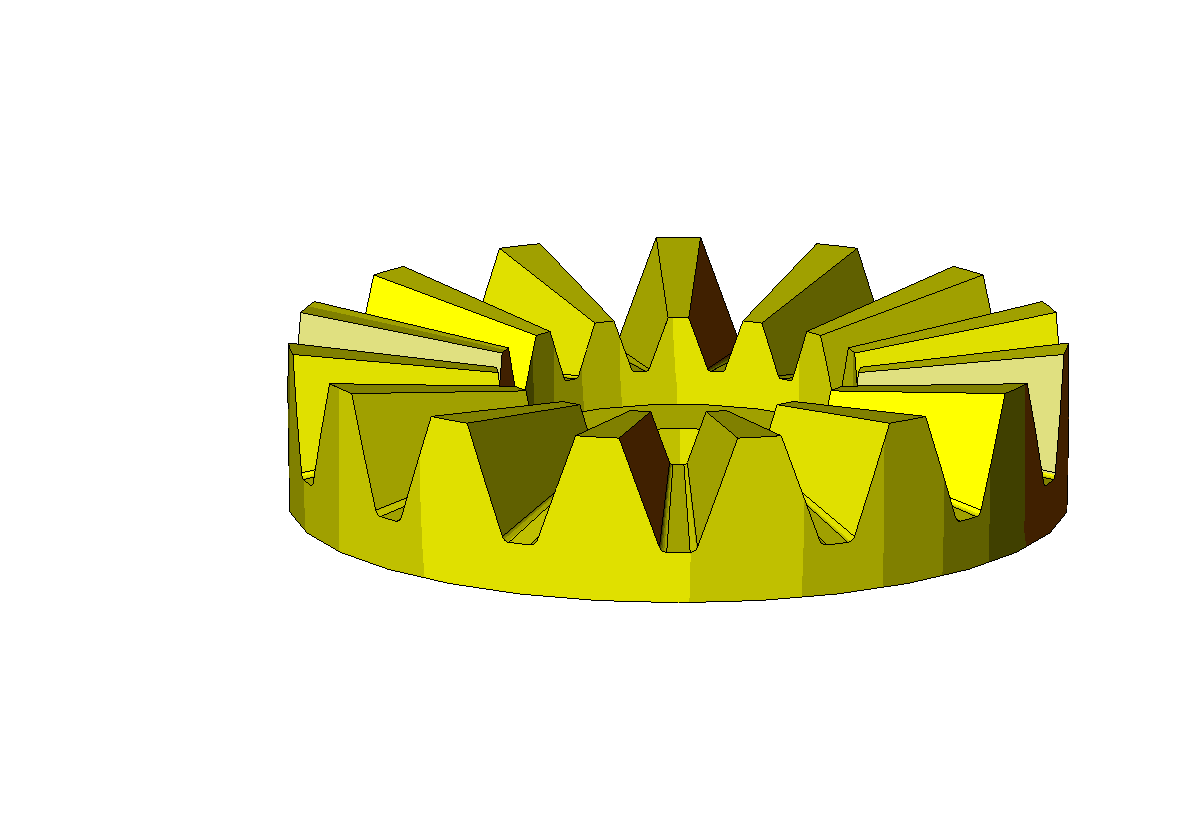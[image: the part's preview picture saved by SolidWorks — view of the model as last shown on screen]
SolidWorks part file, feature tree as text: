
SOLIDWORKS PART (.sldprt)
format: sldprt  version: not decoded by parser v0  size: 763,904 bytes
history: native  units: mm
features: plane x5, sketch x5, material x1, revolve x1, pattern_circular x1, cut_extrude x1 (+10 scaffold rows collapsed)
feature tree (24):
  scaffold x10  (default folders/planes/origin — collapsed)
  material  "Matériau <non spécifié>"
  plane  "Plan1"
  plane  "Plan de creux"
  plane  "Plan3"
  sketch  "def"  dims[c1.D1=10.0mm c1.D2=1.0mm c1.D3=1.0mm c1.D4=0.3mm c1.D5=~14.911604mm c2.D1=15.0mm c2.D6=~8.457328mm c2.D2=2.0mm c2.D7=~6.009154mm c2.D3=1.0mm c2.D8=~2.819109mm c2.D4=0.15mm c2.D5=8.0mm c3.D6=1.0mm c3.D7=85.0mm]
  sketch  "coneprimitif"  dims[c1.D1=~34.995022mm c2.D1=20.0deg c2.D2=~17.690721mm c2.D3=~34.995022mm c3.D3=~7.287182deg c3.D4=~32.161848mm c4.D4=~4.625522deg c4.D5=30.0mm c4.D1=~29.502859mm c5.D1=85.0deg c5.D2=22.0mm c5.D3=~60.444503mm c6.D3=~11.719591deg c7.D3=~64.323697mm c8.D3=~12.680383deg c8.D4=~64.323697mm c9.D4=~5.710593deg c9.D5=25.0mm c9.D6=~9.645009mm c9.D2=20.0mm c10.D5=8.0mm c10.D3=2.0mm c10.D4=4.5mm c10.D1=2.0mm c10.D6=~10.965856mm c10.D2=15.0mm]
  revolve  "conetête"  Angle=360deg
  plane  "plancomplementaire"  Offset=15mm
  sketch  "profil"  dims[c1.D2=0.3mm c1.D1=~112.237132mm c2.D1=20.0deg c2.D3=2.5mm c2.D4=~3.141593mm c2.D5=3.0mm c3.D1=~5.57834mm c4.D1=20.0deg]
  sketch  "centre du cone"
  pattern_circular  "Répétition circulaire1"  Count=15 Angle=360deg
  sketch  "alésage"  dims[c1.D1=~43.425626mm c1.D2=44.0mm c2.D1=14.8mm c2.D2=2.0mm]
  cut_extrude  "centrage"  [1 undecoded]
  plane  "Plan de dent"
decode coverage: 6 of 8 modeling features carry decoded parameters
note: ~ marks probable driven/reference dimensions
note: 1 parameter value undecoded
note: suppression state not decoded; provenance and decode notes live in map.json
